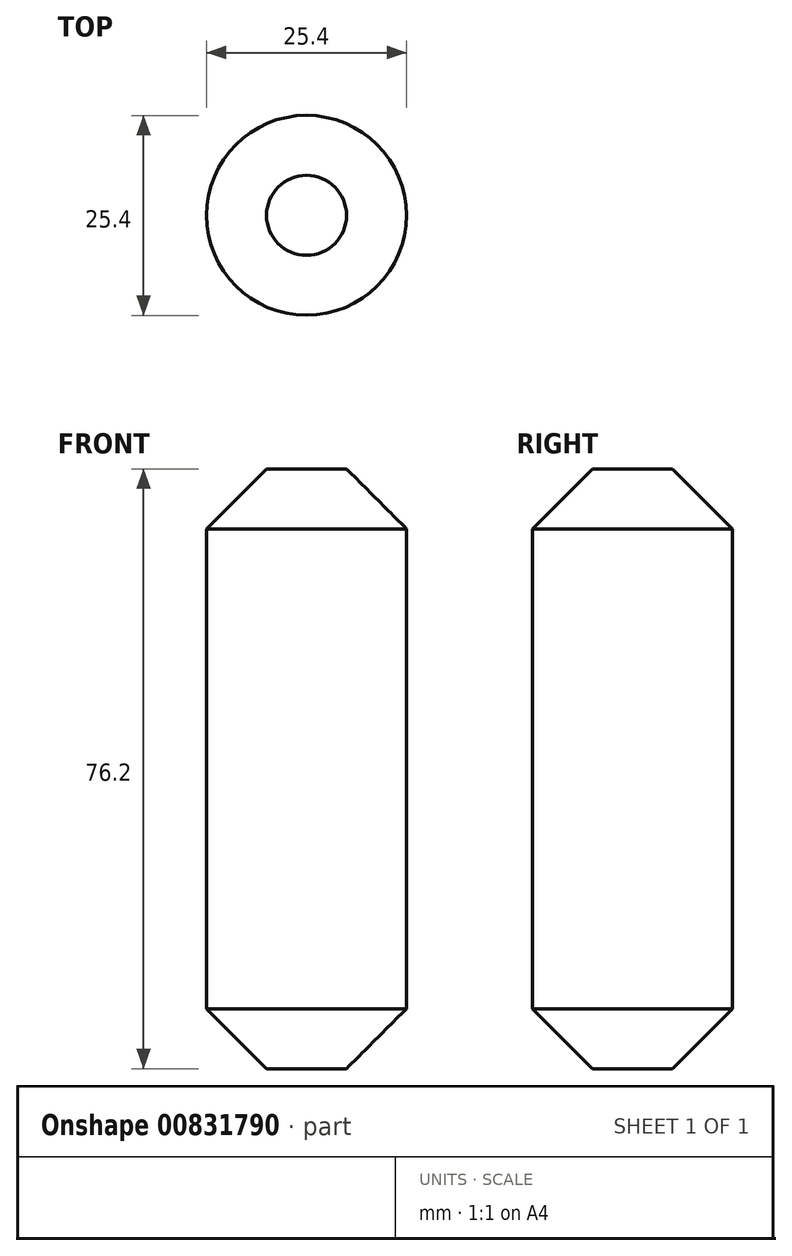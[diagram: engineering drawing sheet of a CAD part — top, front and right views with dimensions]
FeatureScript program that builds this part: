
annotation { "Feature Type Name" : "Feature", "Feature Type Description" : "" }
export const myFeature = defineFeature(function(context is Context, id is Id, definition is map)
    precondition{}
    {
        {
            var Q0;
            Q0=qCreatedBy(makeId("Top.planeOp"),FACE);
            var sketch = newSketch(context, id + "F0", { "sketchPlane" : qUnion([Q0])});
            skCircle(sketch, "E0", {"center": v(-52.3, 54.48) * mm, "radius": 12.7 * mm});
            skSolve(sketch);
        }
        {
            var Q0;
            Q0=makeQuery(id+"F0.imprint","IMPRINT",FACE,{"disambiguationData":[TD([[makeQuery(id+"F0.imprint","IMPRINT",EDGE,{"derivedFrom":sQuery(id+"F0.wireOp",EDGE,"E0")}),1.0]])]});
            extrude(context, id + "F1", {"entities" : qUnion([Q0]), "depth" : 76.2 * mm, "offsetDistance" : 25.4 * mm});
        }
        {
            var Q0;
            Q0=makeQuery(id+"F1.opExtrude","CAP_FACE",FACE,{"disambiguationData":[OSD([sQuery(id+"F0.wireOp",EDGE,"E0")])],"isStart":false});
            chamfer(context, id + "F2", {"entities" : qUnion([Q0]), "width" : 7.62 * mm, "tangentPropagation" : true});
        }
        {
            var Q0;
            Q0=makeQuery(id+"F1.opExtrude","CAP_FACE",FACE,{"disambiguationData":[OSD([sQuery(id+"F0.wireOp",EDGE,"E0")])],"isStart":true});
            chamfer(context, id + "F3", {"entities" : qUnion([Q0]), "width" : 7.62 * mm, "tangentPropagation" : true});
        }
    });
